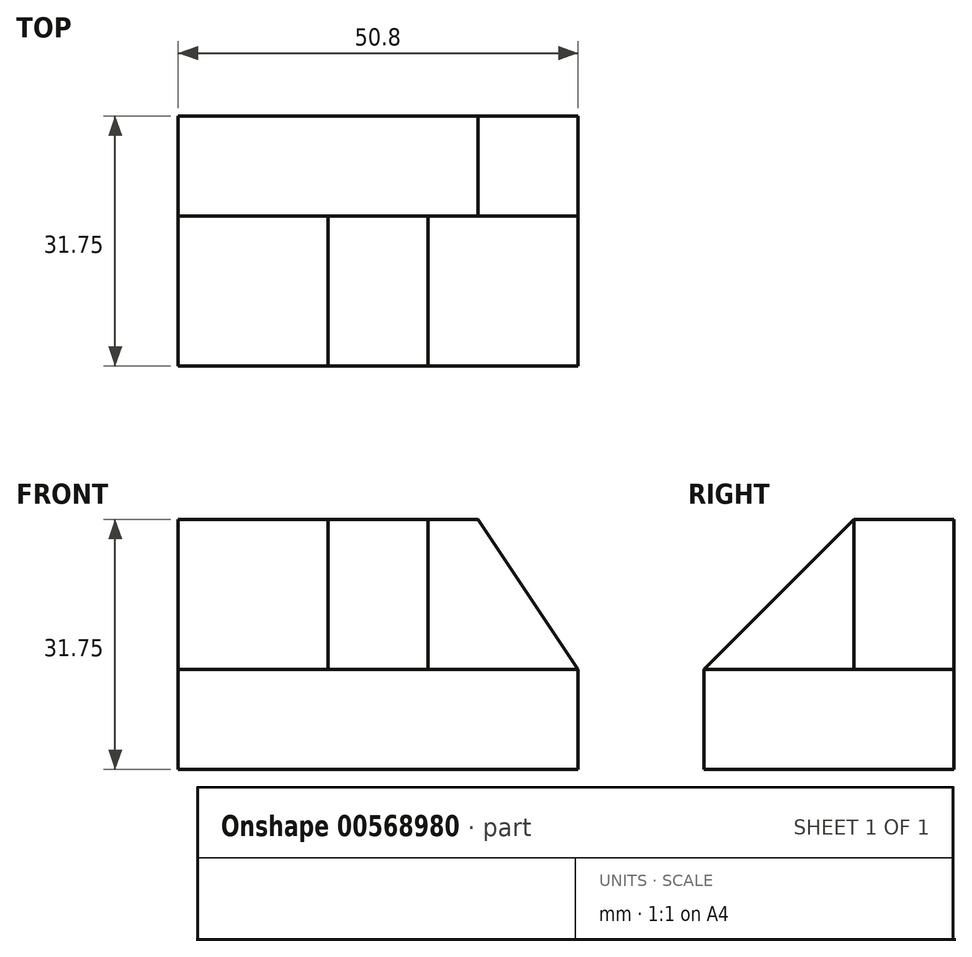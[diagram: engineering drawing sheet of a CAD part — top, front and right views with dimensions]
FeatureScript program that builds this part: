
annotation { "Feature Type Name" : "Feature", "Feature Type Description" : "" }
export const myFeature = defineFeature(function(context is Context, id is Id, definition is map)
    precondition{}
    {
        {
            var Q0;
            Q0=qCreatedBy(makeId("Top.planeOp"),FACE);
            var sketch = newSketch(context, id + "F0", { "sketchPlane" : qUnion([Q0])});
            skLineSegment(sketch, "E0.bottom", {"start": v(-24.55, -31.75) * mm, "end": v(26.25, -31.75) * mm});
            skLineSegment(sketch, "E0.top", {"start": v(-24.55, 0) * mm, "end": v(26.25, 0) * mm});
            skLineSegment(sketch, "E0.left", {"start": v(-24.55, -31.75) * mm, "end": v(-24.55, 0) * mm});
            skLineSegment(sketch, "E0.right", {"start": v(26.25, -31.75) * mm, "end": v(26.25, 0) * mm});
            skSolve(sketch);
        }
        {
            var Q0;
            Q0 = qSketchRegion(id + "F0", true);
            extrude(context, id + "F1", {"entities" : qUnion([Q0]), "depth" : 31.75 * mm, "offsetDistance" : 25.4 * mm});
        }
        {
            var Q0;
            Q0=makeQuery(id+"F1.opExtrude","SWEPT_FACE",FACE,{"disambiguationData":[OSD([sQuery(id+"F0.wireOp",EDGE,"E0.right")])]});
            var sketch = newSketch(context, id + "F2", { "sketchPlane" : qUnion([Q0])});
            skLineSegment(sketch, "E1", {"start": v(-31.75, 31.75) * mm, "end": v(-12.7, 31.75) * mm});
            skLineSegment(sketch, "E2", {"start": v(-12.7, 31.75) * mm, "end": v(-12.7, 12.7) * mm});
            skLineSegment(sketch, "E3", {"start": v(-12.7, 12.7) * mm, "end": v(-31.75, 12.7) * mm});
            skLineSegment(sketch, "E4", {"start": v(-31.75, 12.7) * mm, "end": v(-31.75, 31.75) * mm});
            skSolve(sketch);
        }
        {
            var Q0;
            Q0=makeQuery(id+"F2.imprint","IMPRINT",FACE,{"disambiguationData":[TD([[makeQuery(id+"F2.imprint","IMPRINT",EDGE,{"derivedFrom":sQuery(id+"F2.wireOp",EDGE,"E1")}),-1.0]])]});
            var sketch = newSketch(context, id + "F3", { "sketchPlane" : qUnion([Q0])});
            skSolve(sketch);
        }
        {
            var Q0;
            Q0 = qSketchRegion(id + "F3", true);
            var Q1;
            Q1=makeQuery(id+"F2.imprint","IMPRINT",FACE,{"disambiguationData":[TD([[makeQuery(id+"F2.imprint","IMPRINT",EDGE,{"derivedFrom":sQuery(id+"F2.wireOp",EDGE,"E1")}),-1.0]])]});
            extrude(context, id + "F4", {"entities" : qUnion([Q0, Q1]), "operationType" : NewBodyOperationType.REMOVE, "oppositeDirection" : true, "depth" : 19.05 * mm, "offsetDistance" : 25.4 * mm});
        }
        {
            var Q0;
            Q0=makeQuery(id+"F1.opExtrude","SWEPT_FACE",FACE,{"disambiguationData":[OSD([sQuery(id+"F0.wireOp",EDGE,"E0.left")])]});
            var sketch = newSketch(context, id + "F5", { "sketchPlane" : qUnion([Q0])});
            skLineSegment(sketch, "E5", {"start": v(12.7, 31.75) * mm, "end": v(12.7, 12.7) * mm});
            skLineSegment(sketch, "E6", {"start": v(12.7, 12.7) * mm, "end": v(31.75, 12.7) * mm});
            skLineSegment(sketch, "E7", {"start": v(31.75, 12.7) * mm, "end": v(31.75, 31.75) * mm});
            skLineSegment(sketch, "E8", {"start": v(31.75, 31.75) * mm, "end": v(12.7, 31.75) * mm});
            skSolve(sketch);
        }
        {
            var Q0;
            Q0=makeQuery(id+"F5.imprint","IMPRINT",FACE,{"disambiguationData":[TD([[makeQuery(id+"F5.imprint","IMPRINT",EDGE,{"derivedFrom":sQuery(id+"F5.wireOp",EDGE,"E5")}),1.0]])]});
            var sketch = newSketch(context, id + "F6", { "sketchPlane" : qUnion([Q0])});
            skSolve(sketch);
        }
        {
            var Q0;
            Q0 = qSketchRegion(id + "F6", true);
            var Q1;
            Q1=makeQuery(id+"F5.imprint","IMPRINT",FACE,{"disambiguationData":[TD([[makeQuery(id+"F5.imprint","IMPRINT",EDGE,{"derivedFrom":sQuery(id+"F5.wireOp",EDGE,"E5")}),1.0]])]});
            extrude(context, id + "F7", {"entities" : qUnion([Q0, Q1]), "operationType" : NewBodyOperationType.REMOVE, "oppositeDirection" : true, "depth" : 19.05 * mm, "offsetDistance" : 25.4 * mm});
        }
        {
            var Q0;
            Q0=makeQuery(id+"F7.boolean.opBoolean","COPY",FACE,{"derivedFrom":makeQuery(id+"F7.opExtrude","CAP_FACE",FACE,{"disambiguationData":[OSD([sQuery(id+"F5.wireOp",EDGE,"E5"),sQuery(id+"F5.wireOp",EDGE,"E6"),sQuery(id+"F5.wireOp",EDGE,"E7"),sQuery(id+"F5.wireOp",EDGE,"E8")])],"isStart":false})});
            var sketch = newSketch(context, id + "F8", { "sketchPlane" : qUnion([Q0])});
            skLineSegment(sketch, "E9", {"start": v(12.7, 31.75) * mm, "end": v(31.75, 12.7) * mm});
            skLineSegment(sketch, "E10", {"start": v(31.75, 12.7) * mm, "end": v(31.75, 31.75) * mm});
            skLineSegment(sketch, "E11", {"start": v(31.75, 31.75) * mm, "end": v(12.7, 31.75) * mm});
            skSolve(sketch);
        }
        {
            var Q0;
            Q0=makeQuery(id+"F8.imprint","IMPRINT",FACE,{"disambiguationData":[TD([[makeQuery(id+"F8.imprint","IMPRINT",EDGE,{"derivedFrom":sQuery(id+"F8.wireOp",EDGE,"E9")}),1.0]])]});
            extrude(context, id + "F9", {"entities" : qUnion([Q0]), "operationType" : NewBodyOperationType.REMOVE, "oppositeDirection" : true, "depth" : 12.7 * mm, "offsetDistance" : 25.4 * mm});
        }
        {
            var Q0;
            Q0=makeQuery(id+"F4.boolean.opBoolean","COPY",FACE,{"derivedFrom":makeQuery(id+"F4.opExtrude","SWEPT_FACE",FACE,{"disambiguationData":[OSD([sQuery(id+"F2.wireOp",EDGE,"E2")])]})});
            var sketch = newSketch(context, id + "F10", { "sketchPlane" : qUnion([Q0])});
            skLineSegment(sketch, "E12", {"start": v(13.55, 31.75) * mm, "end": v(26.25, 12.7) * mm});
            skLineSegment(sketch, "E13", {"start": v(26.25, 12.7) * mm, "end": v(26.25, 31.75) * mm});
            skLineSegment(sketch, "E14", {"start": v(26.25, 31.75) * mm, "end": v(13.55, 31.75) * mm});
            skSolve(sketch);
        }
        {
            var Q0;
            Q0=makeQuery(id+"F10.imprint","IMPRINT",FACE,{"disambiguationData":[TD([[makeQuery(id+"F10.imprint","IMPRINT",EDGE,{"derivedFrom":sQuery(id+"F10.wireOp",EDGE,"E12")}),1.0]])]});
            extrude(context, id + "F11", {"entities" : qUnion([Q0]), "operationType" : NewBodyOperationType.REMOVE, "oppositeDirection" : true, "depth" : 12.7 * mm, "offsetDistance" : 25.4 * mm});
        }
    });
